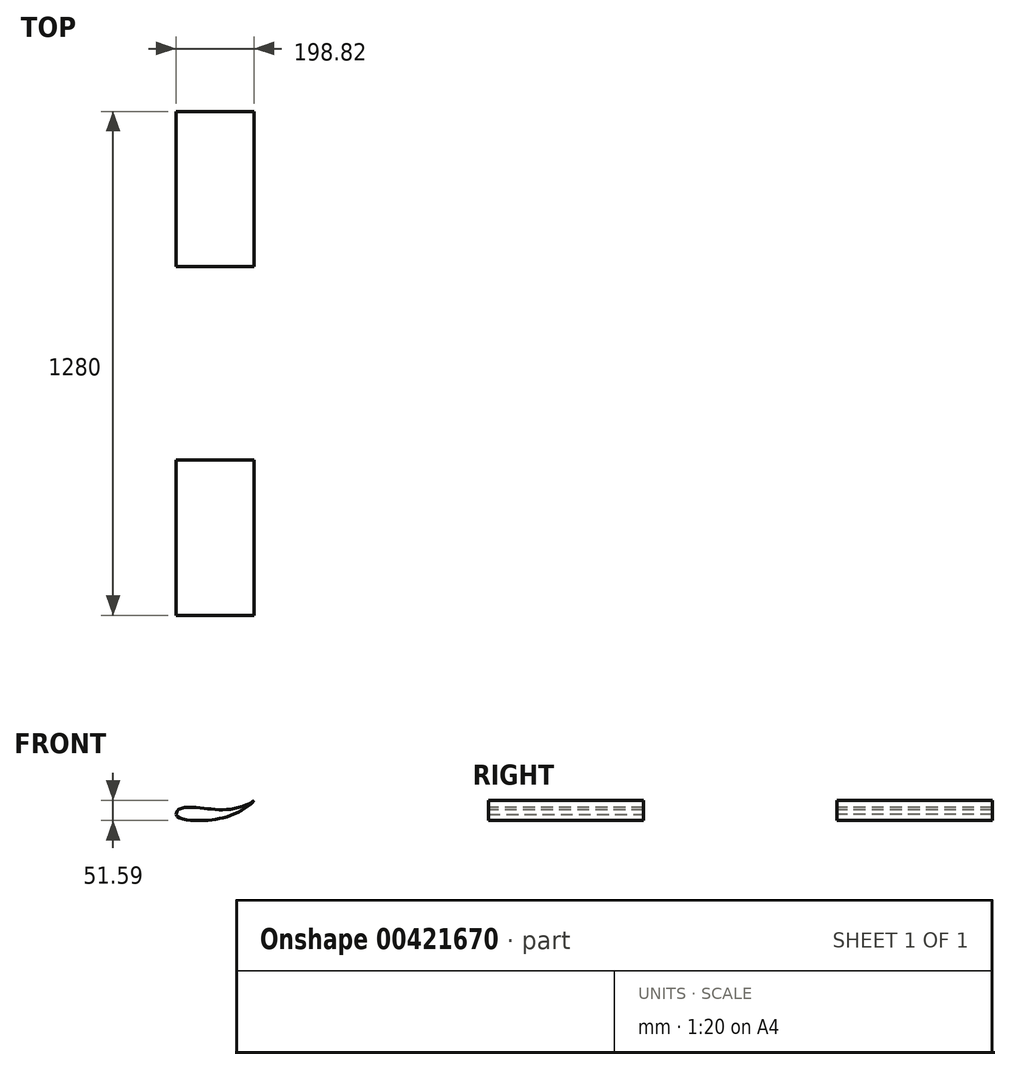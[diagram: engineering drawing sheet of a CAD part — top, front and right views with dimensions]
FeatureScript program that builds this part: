
annotation { "Feature Type Name" : "Feature", "Feature Type Description" : "" }
export const myFeature = defineFeature(function(context is Context, id is Id, definition is map)
    precondition{}
    {
        {
            var Q0;
            Q0=qCreatedBy(makeId("Front.planeOp"),FACE);
            cPlane(context, id + "F0", {"entities" : qUnion([Q0]), "cplaneType" : CPlaneType.OFFSET, "offset" : 246 * mm, "width" : 150 * mm, "height" : 150 * mm});
        }
        {
            var Q0;
            Q0=qCreatedBy(id+"F0.planeOp",FACE);
            var sketch = newSketch(context, id + "F1", { "sketchPlane" : qUnion([Q0])});
            skFitSpline(sketch, "E0", {"points": [v(-1187.91, 182.25) * mm, v(-1140.4, 199.95) * mm, v(-1059.48, 194.35) * mm, v(-989.1, 218.1) * mm], "startDerivative": vector(18.05, 185.68) * mm, "endDerivative": vector(115.84, 108.11) * mm});
            skFitSpline(sketch, "E1", {"points": [v(-1187.91, 182.25) * mm, v(-1124.25, 166.56) * mm, v(-1043.34, 181.8) * mm, v(-989.1, 218.1) * mm], "startDerivative": vector(42.12, -124.24) * mm, "endDerivative": vector(77.76, 121.89) * mm});
            skSolve(sketch);
        }
        {
            var Q0;
            Q0=makeQuery(id+"F1.imprint","IMPRINT",FACE,{"disambiguationData":[TD([[makeQuery(id+"F1.imprint","IMPRINT",EDGE,{"derivedFrom":sQuery(id+"F1.wireOp",EDGE,"E0")}),-1.0]])]});
            extrude(context, id + "F2", {"entities" : qUnion([Q0]), "depth" : 394 * mm});
        }
        {
            var Q0;
            Q0=makeQuery(id+"F2.opExtrude","SWEPT_BODY",BODY,{"disambiguationData":[OSD([sQuery(id+"F1.wireOp",EDGE,"E0"),sQuery(id+"F1.wireOp",EDGE,"E1")])]});
            var Q1;
            Q1=qCreatedBy(makeId("Front.planeOp"),FACE);
            mirror(context, id + "F3", {"entities" : qUnion([Q0]), "mirrorPlane" : qUnion([Q1])});
        }
    });
